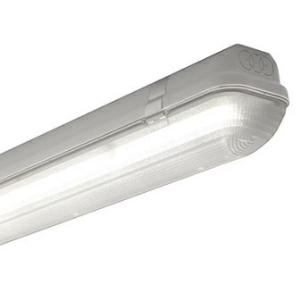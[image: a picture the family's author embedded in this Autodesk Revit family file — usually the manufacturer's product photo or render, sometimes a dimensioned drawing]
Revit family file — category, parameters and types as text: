
# Revit family: 3f_filippi_-_3f_linda_atex_3f_filippi_-_58470_-_3f_linda_led_1x12w_atex_3d_l660
name_source: partatom
category: Lighting Fixtures
units: mm (PartAtom-declared; Revit-internal decimal feet)

## family parameters
Cut with Voids When Loaded = No
Host = Face
Light Source = No
Part Type = Normal
Room Calculation Point = No
Round Connector Dimension = Use Diameter
Shared = No

## types (1)
- 3F Filippi - 3F Linda ATEX (1 x LED, 2033 lm, 14 W, 4000 K)
    Apparent Load = 14 VA
    Approval mark = ENEC
    CIE Flux Codes = 44 77 94 97 100
    Color Rendering = 80
    Color Temperature = 4000 K
    Control Gear = Electronic ballast
    Default Elevation = 1800 mm
    Description = ILLUMINOTECHNICAL
Luminous efficiency 100% (DLOR 97%, ULOR 3%).
Initial luminous flux of the luminaire 2033 lm.
Controlled symmetric distribution.
Installation Interdistance Transv.D = 1.77 x hu - Long.D = 1.17 x hu.
Tabular UGR (CIE 117 - 4H-8H; S=0.25H; 70/50/20): RUG 21.8 - 22.6.
Beam angle: 109° - 64°.
Luminous efficacy 145 lm/W.
Lifetime (L93/B10): 30000 h. (tq+25°C)
Lifetime (L90/B10): 50000 h. (tq+25°C)
Lifetime (L85/B10): 80000 h. (tq+25°C)
Lifetime (L80/B10): 100000 h. (tq+25°C)
Lifetime (L85/B10): 50000 h. (tq+35°C)
Sudden decreased luminous flux after 50000 hours: 0% (C0).
Photobiological safety in compliance with IEC/TR 62778: RG0 risk exempt, (IEC 62471).
In compliance with IEC/EN 62722-2-1 - IEC/EN 62717 standards.

SOURCE
Linear LED module 12W/840.
Energy efficiency class (UE 2019/2020 - UE 2019/2015): D.
CIE 13.3 Colour rendering index: CRI >80 (R9 <50%).
IES TM-30 Fidelity Index: Rf = 84 Rg = 95.
CCT nominal colour temperature 4000 K.
Colour initial tolerance (MacAdam): SDCM 3.

MECHANICAL
Self-extinguishing V2 polycarbonate housing, injection moulded, RAL 7035 grey.
Ecologic anti-aging injected sealing gasket.
Diffuser in self-extinguishing V2 polycarbonate, photo-engraved interior, UV stabilised, injection moulded with smooth outer surface, tamper-proof opening.
Gear-holder reflector in hot-dip galvanised steel, painted with white polyester base.
Snug fit safety snap-lock clips for diffuser mounting in stainless steel, screwdriver opening.
Fixing brackets in stainless steel.
Possibility for technicians to access the interior of the luminaire.
Luminaire with limited surface temperature. - D - (EN 60598-2-24)
Dimensions: 660x100 mm, height 100 mm. Weight 1.2 kg.
IP66 protection degree.
Mechanical strength to impacts IK10 (20 joule).
Glow-wire test resistance 850°C.

ELECTRICAL
Halogen Free electronic wiring 230V-50/60Hz, power factor 0.95, THD <25%, constant output current, SELV, class I, 1 driver.
Power of the luminaire 14 W.
CE - IEC 60598-1 - EN 60598-1.
SAFE FLICKER: PstLM=<1 and SVM=<0.4 (IEC TR 61547-1 and IEC TR 63158), to ensure a more comfortable and safe light.
Luminaire compliant with EN 60598-2-22 for power supply from a centralised emergency system CPSS (Central Power Supply System), not incorporated in the luminaire - high risk areas excluded. The default power and flux are 100% in AC and 100% in DC.
Ambient temperature from -20°C to +35°C.
Temperature class T6 max 85°C.
Entry for power-supply cable through ATEX M20x1,5mm polyamide cable gland, supplied.
Relative humidity UR: <85%.

INSTALLATION
Ceiling / Suspended / Wall.
All accessories dedicated to this product are available on the Catalog and on our website www.3F-Filippi.com.

APPLICATIONS
Environments with ATEX explosive atmosphere (Conformity 2014/34/UE, EN IEC 60079-0, EN 60079-31): Group II, Category 3D (Ex Tc IIIC T85°C Dc).
Suitable product for food production plants (HACCP), IFS (Food Version 6), BRC (GSFS Food Version 7).
Dry, dusty indoor environments, subject to occasional water splashes.
Virtually shatterproof polycarbonate compatibly with the fumes / atmospheres that compromise the elasticity of plastic materials.
Not suitable for installation on surfaces subject to important vibrations, exposed to weather conditions, on ropes or poles.
Suitable for illumination of public car parks and parking grounds referred to DIN 67528:2018-04.

WARNING
Fixture not suitable for cold stores with an ambient temperature <0°C and/or relative humidity >85%.
Luminaire designed for disposal/recycling at end-of-life.
Replaceable (LED only) light source by a professional. Replaceable control gear by a professional.
    Height = 100 mm  [stored 0.328084 ft]
    Lamp = 1 x LED
    Lamp Light Flux = 2033 lm
    Lamp Power = 14 W
    Lamp count = 1
    Length = 660 mm
    Lifetime = 50000 h
    Luminous efficacy = 145 lm/W
    Manufacturer = 3F Filippi
    ModVariant = No
    Model = 3F Filippi - 58470 - 3F Linda LED 1x12W ATEX 3D L660
    Mounting Place = Ceiling
    Mounting Type = Pendant
    Number of Poles = 1
    OnlyDefault = Yes
    Power Factor = 1
    Product Name = 3F Filippi - 3F Linda ATEX
    Product group = pendant luminaire
    ProductGroupID = 9
    Protection Class = Protection class I
    Protection Degree = IP 66
    RLX_Detail_Level = 1
    RLX_Emergency_Light_Flux = 0 lm
    RLX_Emergency_Type = 0
    RLX_Emergency_Type_DB = No
    RlxData = <blob elided: 69389 chars, md5=8b4c96bc>
    Socket = socket
    Standby Power = 0 W
    System Light Flux = 2033 lm
    System Power = 14 W
    Type Comments = Product without accessories
    Type Image = 3ffilippi_3f_linda_led_1x.jpg
    URL = http://relux.com
    VarID = ---
    Voltage = 0 V
    Weight = 0.00 kg
    Width = 100 mm  [stored 0.328084 ft]

note: [stored X ft] marks values corroborated as IEEE doubles in the binary element streams (Revit-internal decimal feet)

## geometry (parser evidence)
native form markers: Blend x4, Sweep x11
no freeform markers — native parametric forms only
